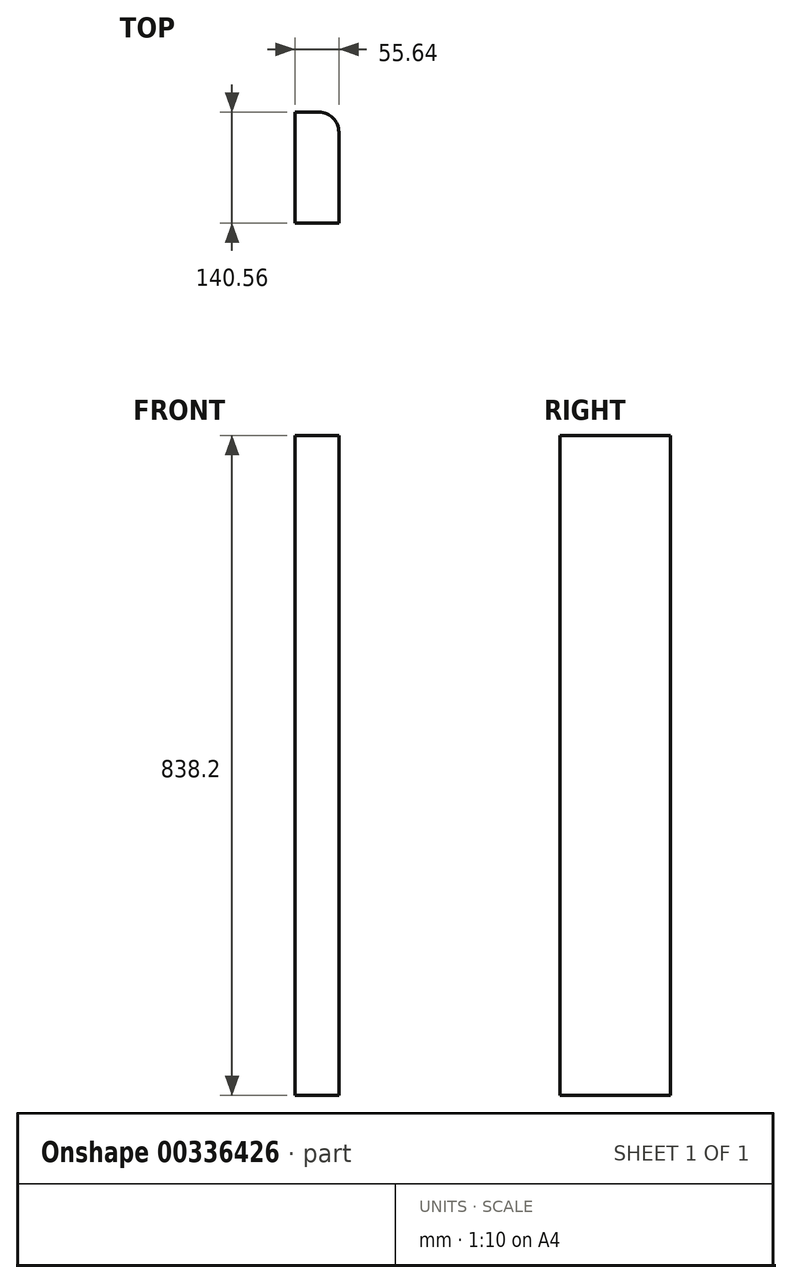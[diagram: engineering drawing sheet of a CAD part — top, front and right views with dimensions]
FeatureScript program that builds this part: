
annotation { "Feature Type Name" : "Feature", "Feature Type Description" : "" }
export const myFeature = defineFeature(function(context is Context, id is Id, definition is map)
    precondition{}
    {
        {
            var Q0;
            Q0=qCreatedBy(makeId("Top.planeOp"),FACE);
            var sketch = newSketch(context, id + "F0", { "sketchPlane" : qUnion([Q0])});
            skLineSegment(sketch, "E0.bottom", {"start": v(0, 0) * mm, "end": v(55.64, 0) * mm});
            skLineSegment(sketch, "E0.top", {"start": v(0, -140.56) * mm, "end": v(55.64, -140.56) * mm});
            skLineSegment(sketch, "E0.left", {"start": v(0, 0) * mm, "end": v(0, -140.56) * mm});
            skLineSegment(sketch, "E0.right", {"start": v(55.64, 0) * mm, "end": v(55.64, -140.56) * mm});
            skSolve(sketch);
        }
        {
            var Q0;
            Q0 = qSketchRegion(id + "F0", true);
            extrude(context, id + "F1", {"entities" : qUnion([Q0]), "depth" : 838.2 * mm});
        }
        {
            var Q0;
            Q0=makeQuery(id+"F1.opExtrude","SWEPT_EDGE",EDGE,{"disambiguationData":[OSD([sQuery(id+"F0.wireOp",EDGE,"E0.bottom"),sQuery(id+"F0.wireOp",EDGE,"E0.right")])]});
            fillet(context, id + "F2", {"entities" : qUnion([Q0]), "radius" : 25.4 * mm, "tangentPropagation" : true, "allowEdgeOverflow" : false});
        }
    });
